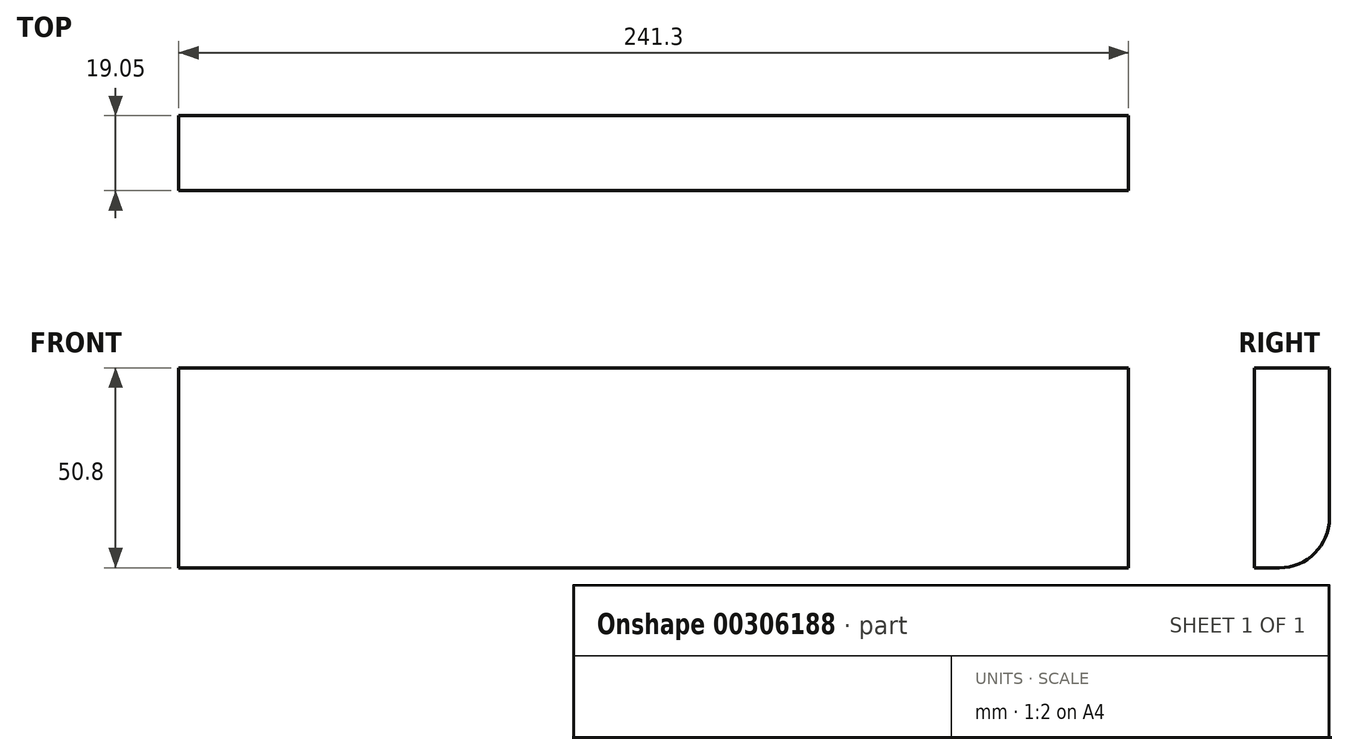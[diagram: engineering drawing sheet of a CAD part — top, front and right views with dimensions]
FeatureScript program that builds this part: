
annotation { "Feature Type Name" : "Feature", "Feature Type Description" : "" }
export const myFeature = defineFeature(function(context is Context, id is Id, definition is map)
    precondition{}
    {
        {
            var Q0;
            Q0=qCreatedBy(makeId("Front.planeOp"),FACE);
            var sketch = newSketch(context, id + "F0", { "sketchPlane" : qUnion([Q0])});
            skLineSegment(sketch, "E0.bottom", {"start": v(120.65, 25.4) * mm, "end": v(-120.65, 25.4) * mm});
            skLineSegment(sketch, "E0.top", {"start": v(120.65, -25.4) * mm, "end": v(-120.65, -25.4) * mm});
            skLineSegment(sketch, "E0.left", {"start": v(120.65, 25.4) * mm, "end": v(120.65, -25.4) * mm});
            skLineSegment(sketch, "E0.right", {"start": v(-120.65, 25.4) * mm, "end": v(-120.65, -25.4) * mm});
            skPoint(sketch, "E0.middle", {"position": v(0, 0) * mm});
            skSolve(sketch);
        }
        {
            var Q0;
            Q0=makeQuery(id+"F0.imprint","IMPRINT",FACE,{"disambiguationData":[TD([[makeQuery(id+"F0.imprint","IMPRINT",EDGE,{"derivedFrom":sQuery(id+"F0.wireOp",EDGE,"E0.bottom")}),1.0]])]});
            extrude(context, id + "F1", {"entities" : qUnion([Q0]), "depth" : 19.05 * mm});
        }
        {
            var Q0;
            Q0=makeQuery(id+"F1.opExtrude","CAP_EDGE",EDGE,{"disambiguationData":[OSD([sQuery(id+"F0.wireOp",EDGE,"E0.top")])],"isStart":true});
            fillet(context, id + "F2", {"entities" : qUnion([Q0]), "radius" : 12.7 * mm, "tangentPropagation" : true, "allowEdgeOverflow" : false});
        }
    });
